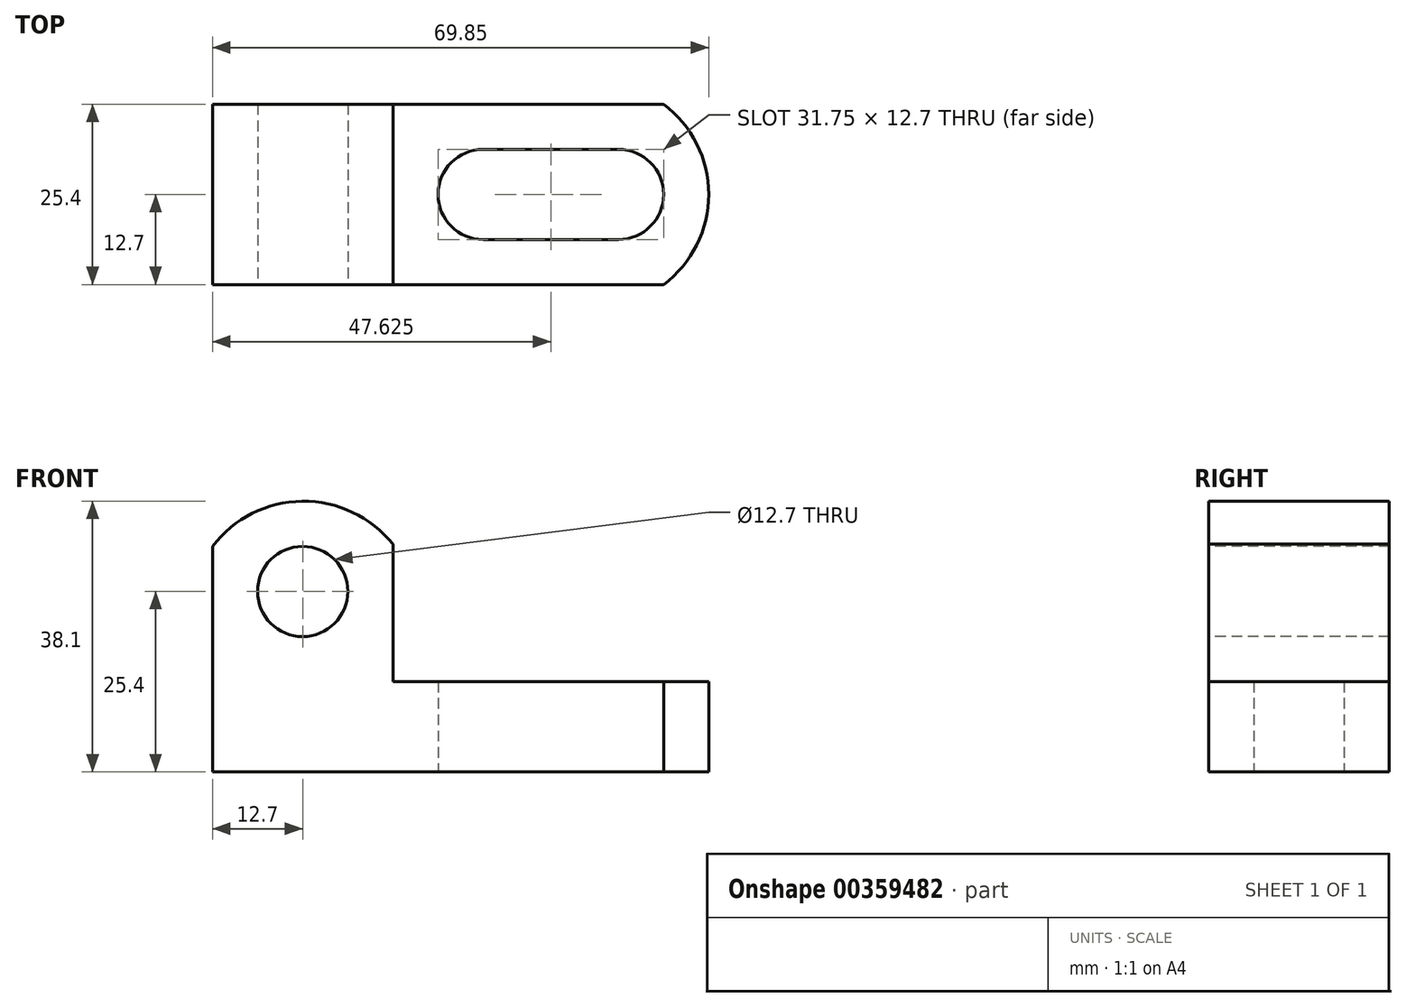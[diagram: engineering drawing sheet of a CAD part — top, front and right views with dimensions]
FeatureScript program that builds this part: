
annotation { "Feature Type Name" : "Feature", "Feature Type Description" : "" }
export const myFeature = defineFeature(function(context is Context, id is Id, definition is map)
    precondition{}
    {
        {
            var Q0;
            Q0=qCreatedBy(makeId("Front.planeOp"),FACE);
            var sketch = newSketch(context, id + "F0", { "sketchPlane" : qUnion([Q0])});
            skLineSegment(sketch, "E0", {"start": v(0, 38.1) * mm, "end": v(0, 0) * mm});
            skLineSegment(sketch, "E1", {"start": v(0, 0) * mm, "end": v(69.85, 0) * mm});
            skLineSegment(sketch, "E2", {"start": v(69.85, 0) * mm, "end": v(69.85, 38.1) * mm});
            skLineSegment(sketch, "E3", {"start": v(69.85, 38.1) * mm, "end": v(0, 38.1) * mm});
            skSolve(sketch);
        }
        {
            var Q0;
            Q0 = qSketchRegion(id + "F0", true);
            extrude(context, id + "F1", {"entities" : qUnion([Q0]), "oppositeDirection" : true, "depth" : 25.4 * mm});
        }
        {
            var Q0;
            Q0=qCreatedBy(makeId("Front.planeOp"),FACE);
            var sketch = newSketch(context, id + "F2", { "sketchPlane" : qUnion([Q0])});
            skLineSegment(sketch, "E4", {"start": v(25.4, 38.1) * mm, "end": v(25.4, 12.7) * mm});
            skLineSegment(sketch, "E5", {"start": v(25.4, 12.7) * mm, "end": v(69.85, 12.7) * mm});
            skLineSegment(sketch, "E6", {"start": v(69.85, 12.7) * mm, "end": v(69.85, 38.1) * mm});
            skLineSegment(sketch, "E7", {"start": v(69.85, 38.1) * mm, "end": v(25.4, 38.1) * mm});
            skSolve(sketch);
        }
        {
            var Q0;
            Q0 = qSketchRegion(id + "F2", true);
            extrude(context, id + "F3", {"entities" : qUnion([Q0]), "operationType" : NewBodyOperationType.REMOVE, "oppositeDirection" : true, "depth" : 25.4 * mm});
        }
        {
            var Q0;
            Q0=qCreatedBy(makeId("Top.planeOp"),FACE);
            var sketch = newSketch(context, id + "F4", { "sketchPlane" : qUnion([Q0])});
            skArc(sketch, "E8", {"start": v(63.5, 0) * mm, "mid": v(69.85, 12.7) * mm, "end": v(63.5, 25.4) * mm});
            skLineSegment(sketch, "E9", {"start": v(63.5, 25.4) * mm, "end": v(69.85, 25.4) * mm});
            skLineSegment(sketch, "E10", {"start": v(69.85, 25.4) * mm, "end": v(69.85, 0) * mm});
            skLineSegment(sketch, "E11", {"start": v(69.85, 0) * mm, "end": v(63.5, 0) * mm});
            skSolve(sketch);
        }
        {
            var Q0;
            Q0 = qSketchRegion(id + "F4", true);
            extrude(context, id + "F5", {"entities" : qUnion([Q0]), "operationType" : NewBodyOperationType.REMOVE, "depth" : 25.4 * mm});
        }
        {
            var Q0;
            Q0=qCreatedBy(makeId("Front.planeOp"),FACE);
            var sketch = newSketch(context, id + "F6", { "sketchPlane" : qUnion([Q0])});
            skArc(sketch, "E12", {"start": v(25.4, 32.04) * mm, "mid": v(12.63, 38.1) * mm, "end": v(0, 31.75) * mm});
            skLineSegment(sketch, "E13", {"start": v(0, 31.75) * mm, "end": v(0, 38.1) * mm});
            skLineSegment(sketch, "E14", {"start": v(0, 38.1) * mm, "end": v(25.4, 38.1) * mm});
            skLineSegment(sketch, "E15", {"start": v(25.4, 38.1) * mm, "end": v(25.4, 32.04) * mm});
            skSolve(sketch);
        }
        {
            var Q0;
            Q0 = qSketchRegion(id + "F6", true);
            extrude(context, id + "F7", {"entities" : qUnion([Q0]), "operationType" : NewBodyOperationType.REMOVE, "oppositeDirection" : true, "depth" : 25.4 * mm});
        }
        {
            var Q0;
            Q0=qCreatedBy(makeId("Top.planeOp"),FACE);
            var sketch = newSketch(context, id + "F8", { "sketchPlane" : qUnion([Q0])});
            skArc(sketch, "E16", {"start": v(38.1, 19.05) * mm, "mid": v(31.75, 12.7) * mm, "end": v(38.1, 6.35) * mm});
            skArc(sketch, "E17", {"start": v(57.15, 6.35) * mm, "mid": v(63.5, 12.7) * mm, "end": v(57.15, 19.05) * mm});
            skLineSegment(sketch, "E18", {"start": v(38.1, 19.05) * mm, "end": v(57.15, 19.05) * mm});
            skLineSegment(sketch, "E19", {"start": v(57.15, 6.35) * mm, "end": v(38.1, 6.35) * mm});
            skSolve(sketch);
        }
        {
            var Q0;
            Q0 = qSketchRegion(id + "F8", true);
            extrude(context, id + "F9", {"entities" : qUnion([Q0]), "operationType" : NewBodyOperationType.REMOVE, "depth" : 25.4 * mm});
        }
        {
            var Q0;
            Q0=qCreatedBy(makeId("Front.planeOp"),FACE);
            var sketch = newSketch(context, id + "F10", { "sketchPlane" : qUnion([Q0])});
            skCircle(sketch, "E20", {"center": v(12.7, 25.4) * mm, "radius": 6.35 * mm});
            skSolve(sketch);
        }
        {
            var Q0;
            Q0 = qSketchRegion(id + "F10", true);
            extrude(context, id + "F11", {"entities" : qUnion([Q0]), "operationType" : NewBodyOperationType.REMOVE, "oppositeDirection" : true, "depth" : 25.4 * mm});
        }
    });
